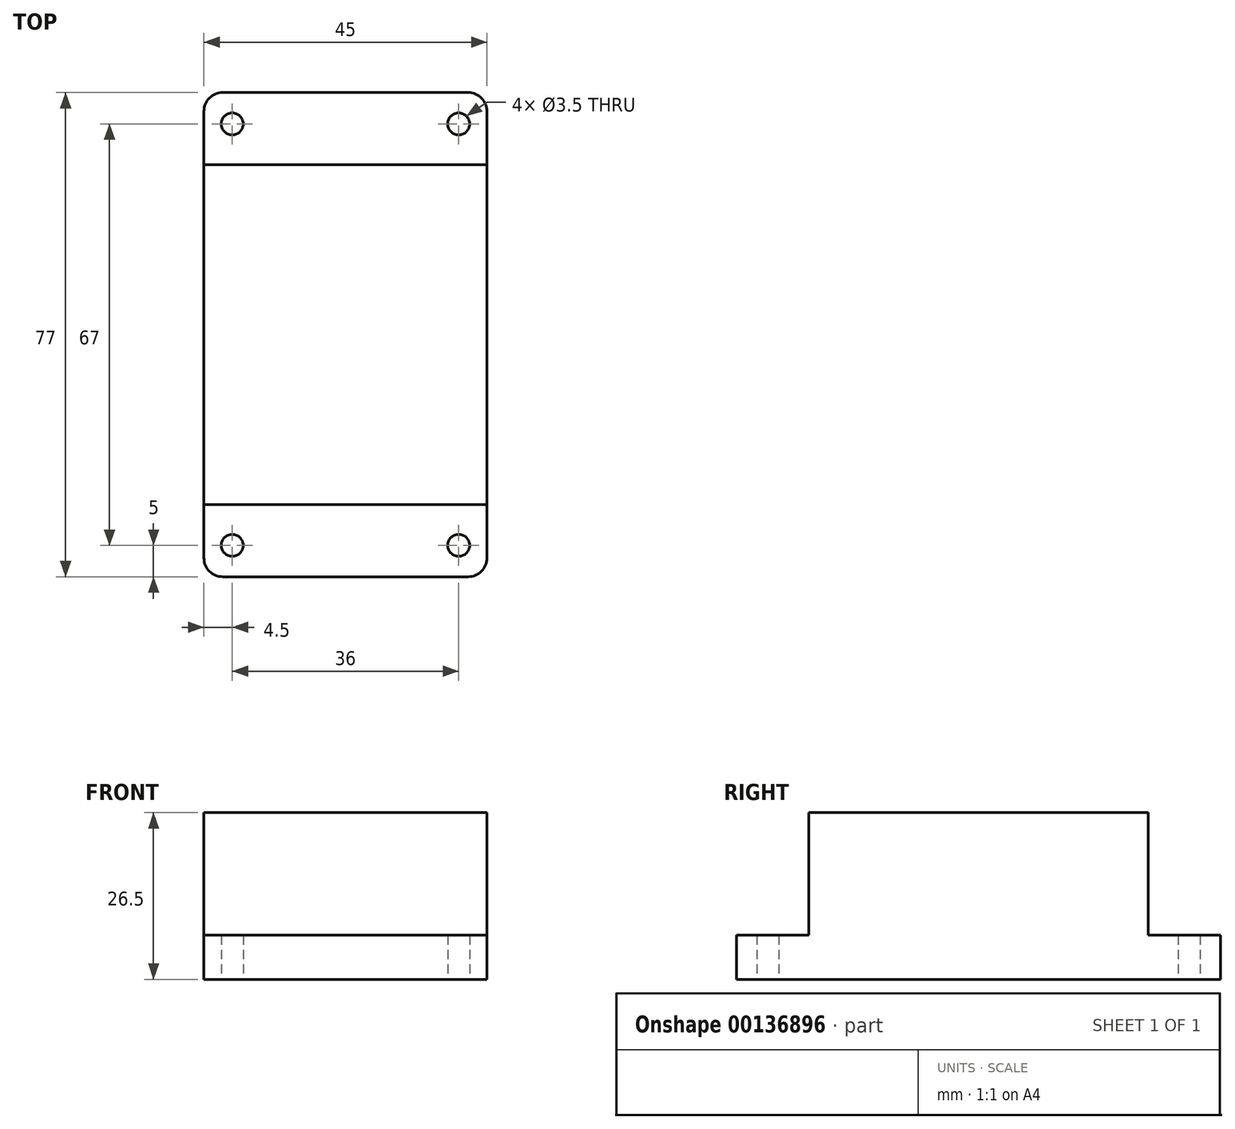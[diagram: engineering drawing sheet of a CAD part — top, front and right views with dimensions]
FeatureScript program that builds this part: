
annotation { "Feature Type Name" : "Feature", "Feature Type Description" : "" }
export const myFeature = defineFeature(function(context is Context, id is Id, definition is map)
    precondition{}
    {
        {
            var Q0;
            Q0=qCreatedBy(makeId("Top.planeOp"),FACE);
            var sketch = newSketch(context, id + "F0", { "sketchPlane" : qUnion([Q0])});
            skLineSegment(sketch, "E0", {"start": v(22.5, -35.5) * mm, "end": v(22.5, 0) * mm});
            skCircle(sketch, "E1", {"center": v(18, -33.5) * mm, "radius": 1.75 * mm});
            skPoint(sketch, "E2.visualSharp", {"position": v(22.5, -38.5) * mm});
            skArc(sketch, "E2.filletArc", {"start": v(19.5, -38.5) * mm, "mid": v(21.62, -37.62) * mm, "end": v(22.5, -35.5) * mm});
            skLineSegment(sketch, "E3", {"start": v(19.5, -38.5) * mm, "end": v(0, -38.5) * mm});
            skArc(sketch, "E4.MirrorCS", {"start": v(-19.5, -38.5) * mm, "mid": v(-21.62, -37.62) * mm, "end": v(-22.5, -35.5) * mm});
            skCircle(sketch, "E5.MirrorC", {"center": v(-18, -33.5) * mm, "radius": 1.75 * mm});
            skLineSegment(sketch, "E6.MirrorCS", {"start": v(-19.5, -38.5) * mm, "end": v(0, -38.5) * mm});
            skLineSegment(sketch, "E7.MirrorCS", {"start": v(-22.5, -35.5) * mm, "end": v(-22.5, 0) * mm});
            skPoint(sketch, "E8.MirrorP", {"position": v(-22.5, -38.5) * mm});
            skArc(sketch, "E9.MirrorCS", {"start": v(19.5, 38.5) * mm, "mid": v(21.62, 37.62) * mm, "end": v(22.5, 35.5) * mm});
            skArc(sketch, "E10.MirrorCS", {"start": v(-19.5, 38.5) * mm, "mid": v(-21.62, 37.62) * mm, "end": v(-22.5, 35.5) * mm});
            skCircle(sketch, "E11.MirrorC", {"center": v(-18, 33.5) * mm, "radius": 1.75 * mm});
            skCircle(sketch, "E12.MirrorC", {"center": v(18, 33.5) * mm, "radius": 1.75 * mm});
            skPoint(sketch, "E13.MirrorP", {"position": v(22.5, 38.5) * mm});
            skLineSegment(sketch, "E14.MirrorCS", {"start": v(-22.5, 35.5) * mm, "end": v(-22.5, 0) * mm});
            skLineSegment(sketch, "E15.MirrorCS", {"start": v(-19.5, 38.5) * mm, "end": v(0, 38.5) * mm});
            skPoint(sketch, "E16.MirrorP", {"position": v(-22.5, 38.5) * mm});
            skLineSegment(sketch, "E17.MirrorCS", {"start": v(19.5, 38.5) * mm, "end": v(0, 38.5) * mm});
            skLineSegment(sketch, "E18.MirrorCS", {"start": v(22.5, 35.5) * mm, "end": v(22.5, 0) * mm});
            skSolve(sketch);
        }
        {
            var Q0;
            Q0=makeQuery(id+"F0.imprint","IMPRINT",FACE,{"disambiguationData":[TD([[makeQuery(id+"F0.imprint","IMPRINT",EDGE,{"derivedFrom":sQuery(id+"F0.wireOp",EDGE,"E0")}),1.0]])]});
            extrude(context, id + "F1", {"entities" : qUnion([Q0]), "depth" : 7 * mm});
        }
        {
            var Q0;
            Q0=makeQuery(id+"F1.opExtrude","CAP_FACE",FACE,{"disambiguationData":[OSD([sQuery(id+"F0.wireOp",EDGE,"E0"),sQuery(id+"F0.wireOp",EDGE,"E1"),sQuery(id+"F0.wireOp",EDGE,"E2.filletArc"),sQuery(id+"F0.wireOp",EDGE,"E3"),sQuery(id+"F0.wireOp",EDGE,"E4.MirrorCS"),sQuery(id+"F0.wireOp",EDGE,"E5.MirrorC"),sQuery(id+"F0.wireOp",EDGE,"E6.MirrorCS"),sQuery(id+"F0.wireOp",EDGE,"E7.MirrorCS"),sQuery(id+"F0.wireOp",EDGE,"E9.MirrorCS"),sQuery(id+"F0.wireOp",EDGE,"E10.MirrorCS"),sQuery(id+"F0.wireOp",EDGE,"E11.MirrorC"),sQuery(id+"F0.wireOp",EDGE,"E12.MirrorC"),sQuery(id+"F0.wireOp",EDGE,"E14.MirrorCS"),sQuery(id+"F0.wireOp",EDGE,"E15.MirrorCS"),sQuery(id+"F0.wireOp",EDGE,"E17.MirrorCS"),sQuery(id+"F0.wireOp",EDGE,"E18.MirrorCS")])],"isStart":false});
            var sketch = newSketch(context, id + "F2", { "sketchPlane" : qUnion([Q0])});
            skLineSegment(sketch, "E19.bottom", {"start": v(-22.5, 27) * mm, "end": v(22.5, 27) * mm});
            skLineSegment(sketch, "E19.top", {"start": v(-22.5, -27) * mm, "end": v(22.5, -27) * mm});
            skLineSegment(sketch, "E19.left", {"start": v(-22.5, 27) * mm, "end": v(-22.5, -27) * mm});
            skLineSegment(sketch, "E19.right", {"start": v(22.5, 27) * mm, "end": v(22.5, -27) * mm});
            skPoint(sketch, "E19.middle", {"position": v(0, 0) * mm});
            skSolve(sketch);
        }
        {
            var Q0;
            Q0=makeQuery(id+"F2.imprint","IMPRINT",FACE,{"disambiguationData":[TD([[makeQuery(id+"F2.imprint","IMPRINT",EDGE,{"derivedFrom":sQuery(id+"F2.wireOp",EDGE,"E19.bottom")}),-1.0]])]});
            extrude(context, id + "F3", {"entities" : qUnion([Q0]), "operationType" : NewBodyOperationType.ADD, "depth" : (26.5 - 7) * mm});
        }
    });
